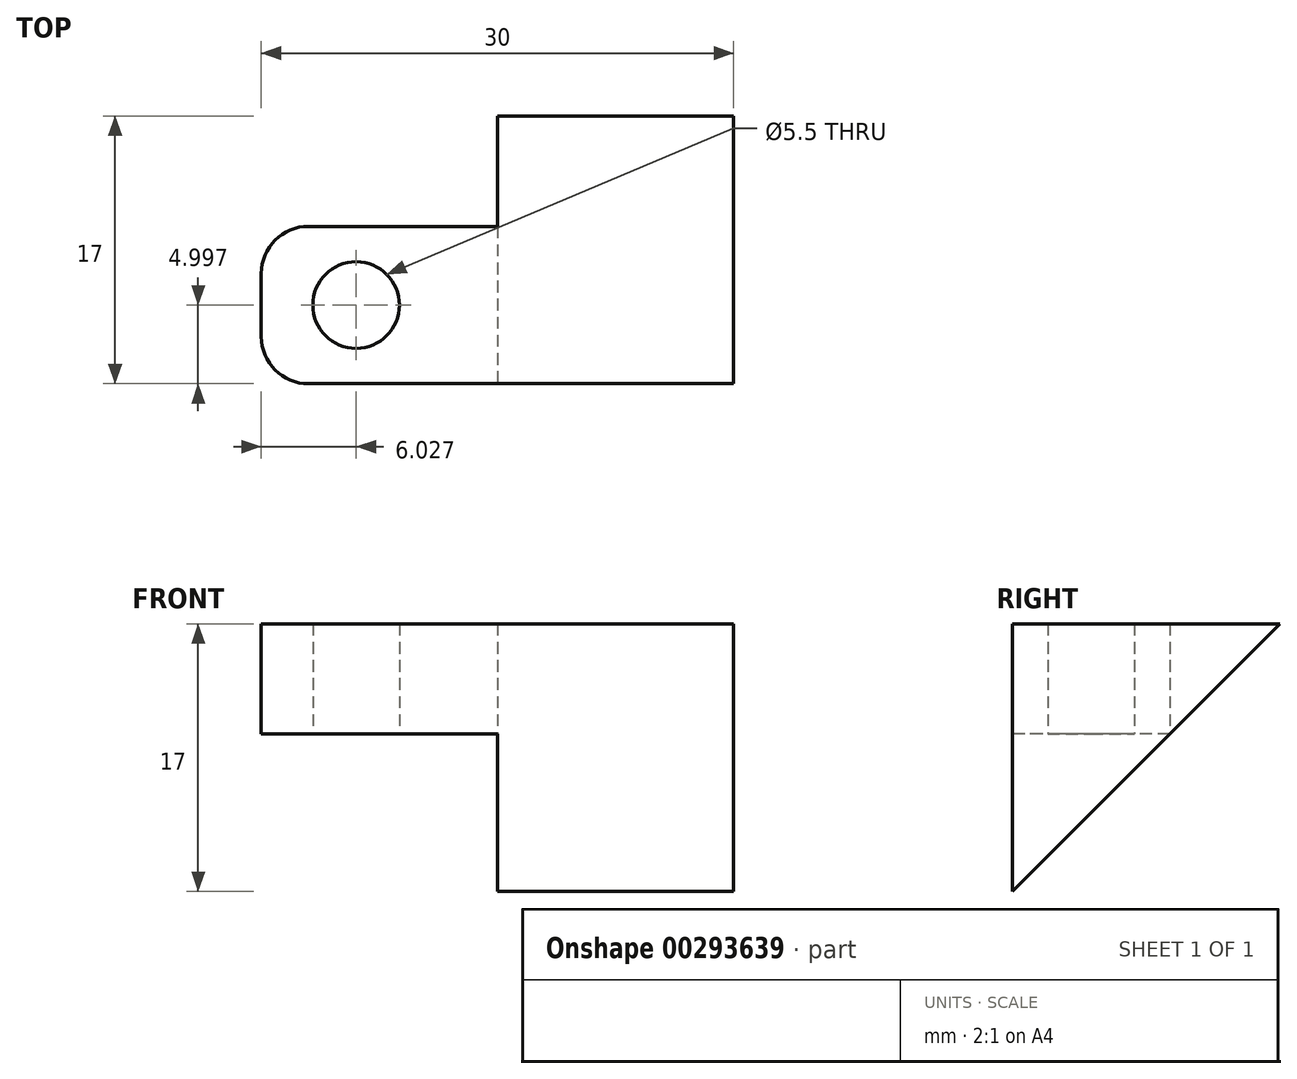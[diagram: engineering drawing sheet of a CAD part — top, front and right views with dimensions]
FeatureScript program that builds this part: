
annotation { "Feature Type Name" : "Feature", "Feature Type Description" : "" }
export const myFeature = defineFeature(function(context is Context, id is Id, definition is map)
    precondition{}
    {
        {
            var Q0;
            Q0=qCreatedBy(makeId("Top.planeOp"),FACE);
            var sketch = newSketch(context, id + "F0", { "sketchPlane" : qUnion([Q0])});
            skCircle(sketch, "E0", {"center": v(-32.3, 35.39) * mm, "radius": 2.75 * mm});
            skLineSegment(sketch, "E1.bottom", {"start": v(-38.33, 40.39) * mm, "end": v(-8.33, 40.39) * mm});
            skLineSegment(sketch, "E1.top", {"start": v(-38.33, 30.39) * mm, "end": v(-8.33, 30.39) * mm});
            skLineSegment(sketch, "E1.left", {"start": v(-38.33, 40.39) * mm, "end": v(-38.33, 30.39) * mm});
            skLineSegment(sketch, "E1.right", {"start": v(-8.33, 40.39) * mm, "end": v(-8.33, 30.39) * mm});
            skSolve(sketch);
        }
        {
            var Q0;
            Q0 = qSketchRegion(id + "F0", true);
            var Q1;
            Q1=makeQuery(id+"F0.imprint","IMPRINT",FACE,{"disambiguationData":[TD([[makeQuery(id+"F0.imprint","IMPRINT",EDGE,{"derivedFrom":sQuery(id+"F0.wireOp",EDGE,"E0")}),-1.0]])]});
            extrude(context, id + "F1", {"entities" : qUnion([Q0, Q1]), "depth" : 7 * mm});
        }
        {
            var Q0;
            Q0=makeQuery(id+"F1.opExtrude","SWEPT_FACE",FACE,{"disambiguationData":[OSD([sQuery(id+"F0.wireOp",EDGE,"E1.right")])]});
            var sketch = newSketch(context, id + "F2", { "sketchPlane" : qUnion([Q0])});
            skLineSegment(sketch, "E2", {"start": v(40.39, 0) * mm, "end": v(30.39, -10) * mm});
            skLineSegment(sketch, "E3", {"start": v(30.39, -10) * mm, "end": v(30.39, 0) * mm});
            skLineSegment(sketch, "E4", {"start": v(30.39, 0) * mm, "end": v(40.39, 0) * mm});
            skLineSegment(sketch, "E5", {"start": v(40.39, 0) * mm, "end": v(47.39, 7) * mm});
            skLineSegment(sketch, "E6", {"start": v(47.39, 7) * mm, "end": v(40.39, 7) * mm});
            skSolve(sketch);
        }
        {
            var Q0;
            Q0 = qSketchRegion(id + "F2", true);
            var Q1;
            Q1=makeQuery(id+"F2.imprint","IMPRINT",FACE,{"disambiguationData":[TD([[makeQuery(id+"F2.imprint","IMPRINT",EDGE,{"derivedFrom":sQuery(id+"F2.wireOp",EDGE,"btEUOGpy-5sJs-MWHj-Dukd-CoRp2hPBxc8p")}),-1.0]])]});
            var Q2;
            Q2=makeQuery(id+"F2.imprint","IMPRINT",FACE,{"disambiguationData":[TD([[makeQuery(id+"F2.imprint","IMPRINT",EDGE,{"derivedFrom":sQuery(id+"F2.wireOp",EDGE,"mEqJkWJR-fYOb-jL2o-m596-578tOy3uQEqF")}),1.0]])]});
            var Q3;
            Q3=makeQuery(id+"F2.imprint","IMPRINT",FACE,{"disambiguationData":[TD([[makeQuery(id+"F2.imprint","IMPRINT",EDGE,{"derivedFrom":sQuery(id+"F2.wireOp",EDGE,"E5")}),1.0]])]});
            extrude(context, id + "F3", {"entities" : qUnion([Q0, Q1, Q2, Q3]), "operationType" : NewBodyOperationType.ADD, "oppositeDirection" : true, "depth" : 15 * mm});
        }
        {
            var Q0;
            Q0=makeQuery(id+"F1.opExtrude","SWEPT_EDGE",EDGE,{"disambiguationData":[OSD([sQuery(id+"F0.wireOp",EDGE,"E1.bottom"),sQuery(id+"F0.wireOp",EDGE,"E1.left")])]});
            var Q1;
            Q1=makeQuery(id+"F1.opExtrude","SWEPT_EDGE",EDGE,{"disambiguationData":[OSD([sQuery(id+"F0.wireOp",EDGE,"E1.top"),sQuery(id+"F0.wireOp",EDGE,"E1.left")])]});
            fillet(context, id + "F4", {"entities" : qUnion([Q0, Q1]), "radius" : 3 * mm, "tangentPropagation" : true, "allowEdgeOverflow" : false});
        }
        {
            var Q0;
            Q0=makeQuery(id+"F3.boolean.opBoolean","MERGE",FACE,{"derivedFrom":[makeQuery(id+"F3.opExtrude","SWEPT_FACE",FACE,{"disambiguationData":[OSD([sQuery(id+"F2.wireOp",EDGE,"E2")])]}),makeQuery(id+"F3.opExtrude","SWEPT_FACE",FACE,{"disambiguationData":[OSD([sQuery(id+"F2.wireOp",EDGE,"E5")])]})]});
            var sketch = newSketch(context, id + "F5", { "sketchPlane" : qUnion([Q0])});
            skCircle(sketch, "E7", {"center": v(-15.83, -35.02) * mm, "radius": 1.5 * mm});
            skPoint(sketch, "E7.centerSnap0", {"position": v(-15.83, -38.46) * mm});
            skSolve(sketch);
        }
        {
            var Q0;
            Q0=makeQuery(id+"F5.imprint","IMPRINT",FACE,{"disambiguationData":[TD([[makeQuery(id+"F5.imprint","IMPRINT",EDGE,{"derivedFrom":sQuery(id+"F5.wireOp",EDGE,"E7")}),1.0]])]});
            extrude(context, id + "F6", {"entities" : qUnion([Q0]), "operationType" : NewBodyOperationType.REMOVE, "oppositeDirection" : true, "depth" : 25 * mm});
        }
    });
